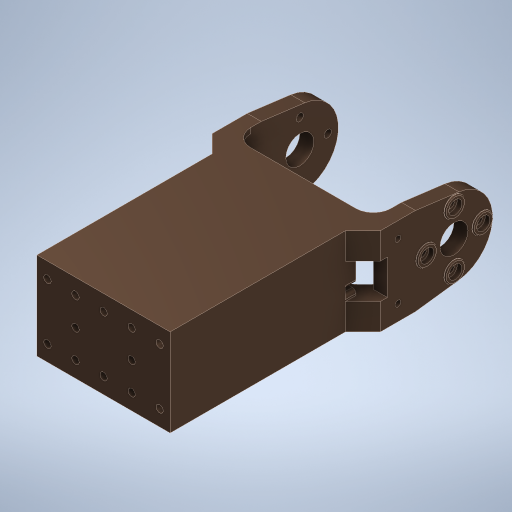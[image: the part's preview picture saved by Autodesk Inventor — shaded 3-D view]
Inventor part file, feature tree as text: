
AUTODESK INVENTOR PART (.ipt)
format: ipt  version: 2024 (Build 280153000, 153)  size: 597,504 bytes
history: native  units: in
note: dims shown in document units (in); Inventor stores cm internally (conversion verified against a paired STEP export)
features: other x2, direct_edit x1, extrude x1, sketch x1, imported_body x1
ambient origin geometry x8: Origin, YZ Plane, XZ Plane, XY Plane, X Axis, Y Axis, Z Axis, Center Point
bodies: Solid1 (feature_tree)
feature tree (6):
  direct_edit  "Direct Edit1"
  extrude  "Extrusion1"  Depth=0.0394in
  sketch  "Sketch1"  dims[d1=0.0394in d2=0.0394in d3=1.9685in d4=0.0in]
  imported_body  "Base1"
  other  "Size1"
  other  "Size2"
